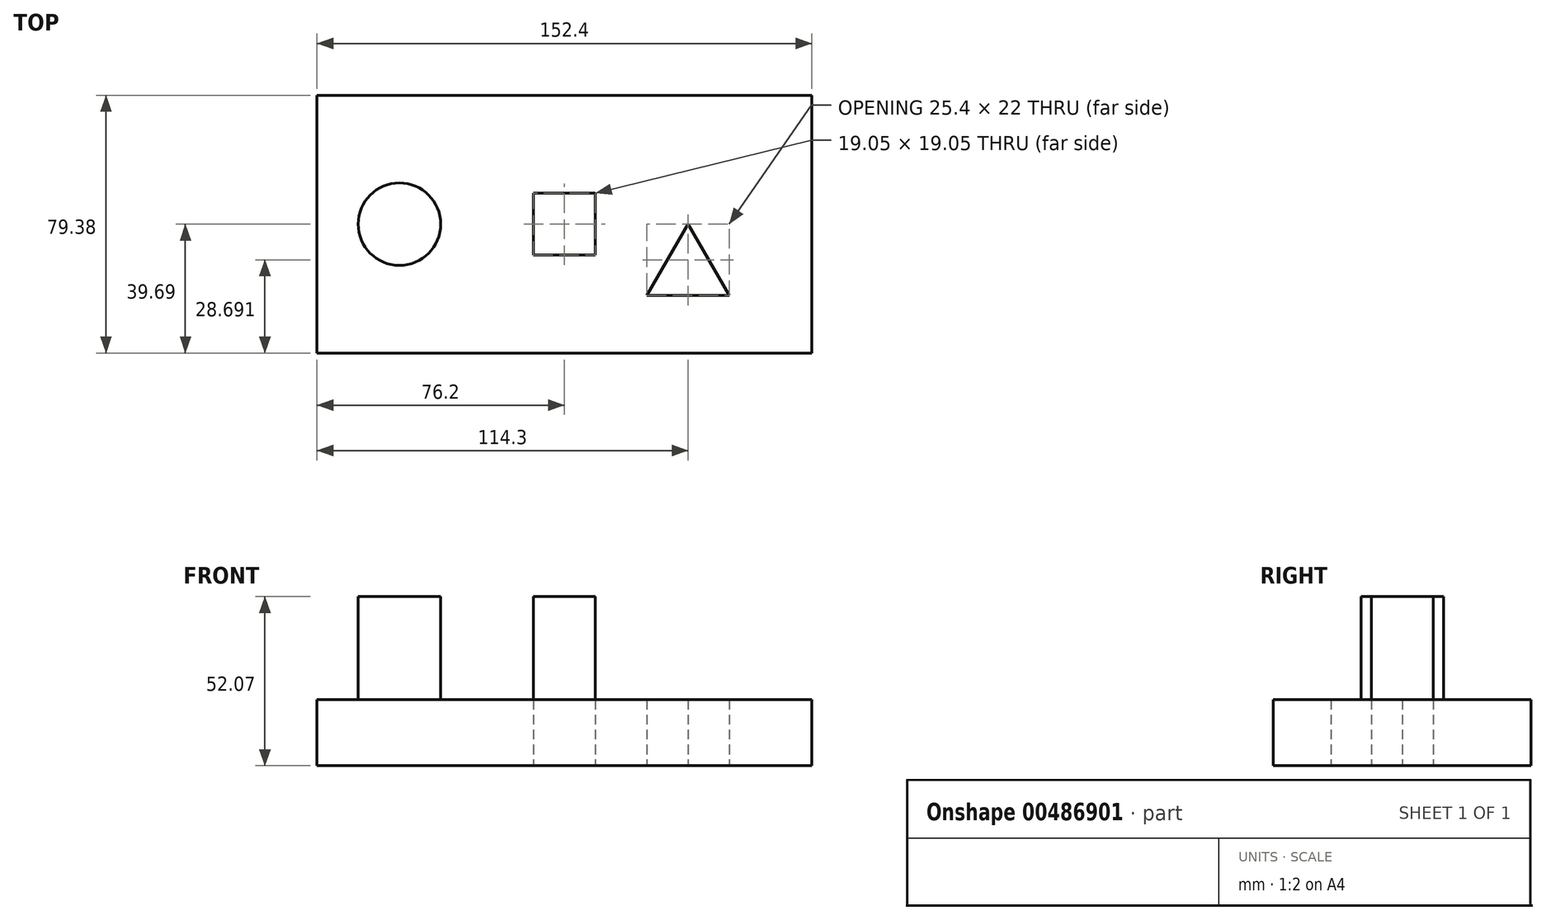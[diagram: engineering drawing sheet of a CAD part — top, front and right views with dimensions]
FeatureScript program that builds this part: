
annotation { "Feature Type Name" : "Feature", "Feature Type Description" : "" }
export const myFeature = defineFeature(function(context is Context, id is Id, definition is map)
    precondition{}
    {
        {
            var Q0;
            Q0=qCreatedBy(makeId("Top.planeOp"),FACE);
            var sketch = newSketch(context, id + "F0", { "sketchPlane" : qUnion([Q0])});
            skPoint(sketch, "E0", {"position": v(0, 0) * mm});
            skPoint(sketch, "E1", {"position": v(6.35, 0) * mm});
            skLineSegment(sketch, "E2", {"start": v(6.35, 0) * mm, "end": v(-6.35, -22) * mm});
            skLineSegment(sketch, "E3", {"start": v(-6.35, -22) * mm, "end": v(19.05, -22) * mm});
            skLineSegment(sketch, "E4", {"start": v(19.05, -22) * mm, "end": v(6.35, 0) * mm});
            skPoint(sketch, "E5", {"position": v(-31.75, 0) * mm});
            skLineSegment(sketch, "E6.bottom", {"start": v(-22.23, -9.53) * mm, "end": v(-41.27, -9.52) * mm});
            skLineSegment(sketch, "E6.top", {"start": v(-22.22, 9.53) * mm, "end": v(-41.27, 9.53) * mm});
            skLineSegment(sketch, "E6.left", {"start": v(-22.23, -9.53) * mm, "end": v(-22.23, 9.53) * mm});
            skLineSegment(sketch, "E6.right", {"start": v(-41.28, -9.52) * mm, "end": v(-41.27, 9.53) * mm});
            skPoint(sketch, "E7", {"position": v(-82.55, 0) * mm});
            skPoint(sketch, "E7.positionSnap0", {"position": v(-41.27, 0) * mm});
            skCircle(sketch, "E8", {"center": v(-82.55, 0) * mm, "radius": 12.7 * mm});
            skPoint(sketch, "E9", {"position": v(44.45, 0) * mm});
            skPoint(sketch, "E10", {"position": v(44.45, 39.69) * mm});
            skPoint(sketch, "E11", {"position": v(44.45, -39.69) * mm});
            skLineSegment(sketch, "E12", {"start": v(44.45, 39.69) * mm, "end": v(44.45, -42.04) * mm});
            skLineSegment(sketch, "E13.bottom", {"start": v(44.45, 39.69) * mm, "end": v(-107.95, 39.69) * mm});
            skLineSegment(sketch, "E13.top", {"start": v(44.45, -39.69) * mm, "end": v(-107.95, -39.69) * mm});
            skLineSegment(sketch, "E13.left", {"start": v(44.45, 39.69) * mm, "end": v(44.45, -39.69) * mm});
            skLineSegment(sketch, "E13.right", {"start": v(-107.95, 39.69) * mm, "end": v(-107.95, -39.69) * mm});
            skSolve(sketch);
        }
        {
            var Q0;
            Q0=makeQuery(id+"F0.imprint","IMPRINT",FACE,{"disambiguationData":[TD([[makeQuery(id+"F0.imprint","IMPRINT",EDGE,{"derivedFrom":sQuery(id+"F0.wireOp",EDGE,"E2")}),-1.0]])]});
            extrude(context, id + "F1", {"entities" : qUnion([Q0]), "depth" : 20.32 * mm});
        }
        {
            var Q0;
            Q0=makeQuery(id+"F0.imprint","IMPRINT",FACE,{"disambiguationData":[TD([[makeQuery(id+"F0.imprint","IMPRINT",EDGE,{"derivedFrom":sQuery(id+"F0.wireOp",EDGE,"E8")}),1.0]])]});
            extrude(context, id + "F2", {"entities" : qUnion([Q0]), "operationType" : NewBodyOperationType.ADD, "depth" : 52.07 * mm});
        }
        {
            var Q0;
            Q0=makeQuery(id+"F1.opExtrude","CAP_FACE",FACE,{"disambiguationData":[OSD([sQuery(id+"F0.wireOp",EDGE,"E2"),sQuery(id+"F0.wireOp",EDGE,"E3"),sQuery(id+"F0.wireOp",EDGE,"E4"),sQuery(id+"F0.wireOp",EDGE,"E6.bottom"),sQuery(id+"F0.wireOp",EDGE,"E6.top"),sQuery(id+"F0.wireOp",EDGE,"E6.left"),sQuery(id+"F0.wireOp",EDGE,"E6.right"),sQuery(id+"F0.wireOp",EDGE,"E8"),sQuery(id+"F0.wireOp",EDGE,"E13.bottom"),sQuery(id+"F0.wireOp",EDGE,"E13.top"),sQuery(id+"F0.wireOp",EDGE,"E13.left"),sQuery(id+"F0.wireOp",EDGE,"E13.right")])],"isStart":false});
            var sketch = newSketch(context, id + "F3", { "sketchPlane" : qUnion([Q0])});
            skSolve(sketch);
        }
        {
            var Q0;
            Q0 = qSketchRegion(id + "F3", true);
            var Q1;
            Q1=makeQuery(id+"F3.imprint","IMPRINT",FACE,{"disambiguationData":[TD([[makeQuery(id+"F3.imprint","IMPRINT",EDGE,{"derivedFrom":makeQuery(id+"F1.opExtrude","CAP_EDGE",EDGE,{"disambiguationData":[OSD([sQuery(id+"F0.wireOp",EDGE,"E6.bottom")])],"isStart":false})}),-1.0]])]});
            extrude(context, id + "F4", {"entities" : qUnion([Q0, Q1]), "depth" : 31.75 * mm});
        }
    });
